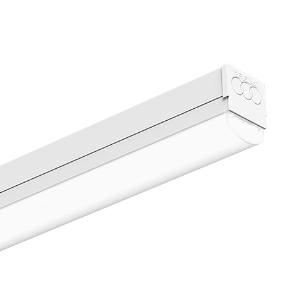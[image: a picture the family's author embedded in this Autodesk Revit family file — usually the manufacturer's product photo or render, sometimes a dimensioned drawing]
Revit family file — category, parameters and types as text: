
# Revit family: 3f_filippi_-_3f_zeta_d_3f_filippi_-_10980_-_3f_zeta_d_1x22_led_ep_l1489
name_source: partatom
category: Lighting Fixtures
units: mm (PartAtom-declared; Revit-internal decimal feet)

## family parameters
Cut with Voids When Loaded = No
Host = Face
Light Source = No
Part Type = Normal
Room Calculation Point = No
Round Connector Dimension = Use Diameter
Shared = No

## types (1)
- 3F Filippi - 3F Zeta D (1 x LED, 3118 lm, 25.5 W, 4000 K)
    Apparent Load = 26 VA
    Approval mark = ENEC
    CIE Flux Codes = 42 71 90 91 100
    Color Rendering = 80
    Color Temperature = 4000 K
    Control Gear = Electronic ballast
    Default Elevation = 1800 mm
    Description = ILLUMINOTECHNICAL
Luminous efficiency 100% (DLOR 91%, ULOR 9%).
Initial luminous flux of the luminaire 3118 lm.
Emergency luminaire luminous flux BLF 15.2%.
Diffused symmetric distribution.
Installation Interdistance Transv.D = 1.31 x hu - Long.D = 1.25 x hu.
Tabular UGR (CIE 117 - 4H-8H; S=0.25H; 70/50/20): RUG 23.8 - 22.2.
Beam angle: 130° - 112°.
Luminous efficacy 122 lm/W.
Lifetime (L93/B10): 30000 h. (tq+25°C)
Lifetime (L90/B10): 50000 h. (tq+25°C)
Lifetime (L85/B10): 80000 h. (tq+25°C)
Lifetime (L80/B10): 100000 h. (tq+25°C)
Sudden decreased luminous flux after 50000 hours: 0% (C0).
Photobiological safety in compliance with IEC/TR 62778: RG0 risk exempt, (IEC 62471).
In compliance with IEC/EN 62722-2-1 - IEC/EN 62717 standards.

SOURCE
Linear LED module 22W/840.
Energy efficiency class (UE 2019/2020 - UE 2019/2015): D.
CIE 13.3 Colour rendering index: CRI >80 (R9 <50%).
IES TM-30 Fidelity Index: Rf = 84 Rg = 95.
CCT nominal colour temperature 4000 K.
Colour initial tolerance (MacAdam): SDCM 3.

MECHANICAL
Housing in hot-galvanised steel, painted in white polyester, obtained through rolling process.
Light unit in hot-galvanised steel, painted in white polyester base with fixing springs and retractable safety hooks in stainless steel.
Curved screen in self-extinguishing polycarbonate, UV stabilised, opal, with smooth outer surface.
End caps in white polycarbonate.
Pair of stainless steel sliding brackets with sliding block screws.
Luminaire with limited surface temperature. - D - (EN 60598-2-24)
Dimensions: 1489x62 mm, height 81 mm. Weight 4.56 kg.
IP40 protection degree.
Mechanical strength to impacts IK06 (1 joule).
Glow-wire test resistance 850°C.

ELECTRICAL
Halogen Free electronic wiring 230V-50/60Hz, power factor 0.85, THD <25%, constant output current, SELV, class I, 1 driver.
Power of the luminaire 25.5 W.
CE - IEC 60598-1 - EN 60598-1.
EP maintained emergency wiring on board, 1h duration, 24h recharge; compliant with EN 60598-2-22, excluding high risk areas.
SAFE FLICKER: PstLM=<1 and SVM=<0.4 (IEC TR 61547-1 and IEC TR 63158), to ensure a more comfortable and safe light.
Ambient temperature from +5°C to +25°C.
Temperature class T6 max 85°C.
Relative humidity UR: <85%.

INSTALLATION
Ceiling / Suspended / Wall.
All accessories dedicated to this product are available on the Catalog and on our website www.3F-Filippi.com.

APPLICATIONS
Suitable product for food production plants (HACCP), IFS (Food Version 6), BRC (GSFS Food Version 7).
In commercial environments, exhibition areas, shops and stores.

WARNING
Luminaire designed for disposal/recycling at end-of-life.
Replaceable (LED only) light source by a professional. Replaceable control gear by a professional.
    Height = 81 mm
    Lamp = 1 x LED
    Lamp Light Flux = 3118 lm
    Lamp Power = 25.5 W
    Lamp count = 1
    Length = 1489 mm
    Lifetime = 50000 h
    Luminous efficacy = 122 lm/W
    Manufacturer = 3F Filippi
    ModVariant = No
    Model = 3F Filippi - 10980 - 3F Zeta D 1x22 LED EP L1489
    Mounting Place = Ceiling
    Mounting Type = Pendant
    Number of Poles = 1
    OnlyDefault = Yes
    Power Factor = 1
    Product Name = 3F Filippi - 3F Zeta D
    Product group = pendant luminaire
    ProductGroupID = 9
    Protection Class = Protection class I
    Protection Degree = IP 40
    RLX_Detail_Level = 1
    RLX_Emergency_Light_Flux = 0 lm
    RLX_Emergency_Type = 0
    RLX_Emergency_Type_DB = No
    RlxData = <blob elided: 33029 chars, md5=e733be59>
    Socket = socket
    Standby Power = 0 W
    System Light Flux = 3118 lm
    System Power = 26 W
    Type Comments = Product without accessories
    Type Image = 3ffilippi_3f_zeta_d.jpg
    URL = http://relux.com
    VarID = ---
    Voltage = 0 V
    Weight = 0.00 kg
    Width = 62 mm  [stored 0.203412 ft]

note: [stored X ft] marks values corroborated as IEEE doubles in the binary element streams (Revit-internal decimal feet)

## geometry (parser evidence)
native form markers: Blend x4, Sweep x12
no freeform markers — native parametric forms only
